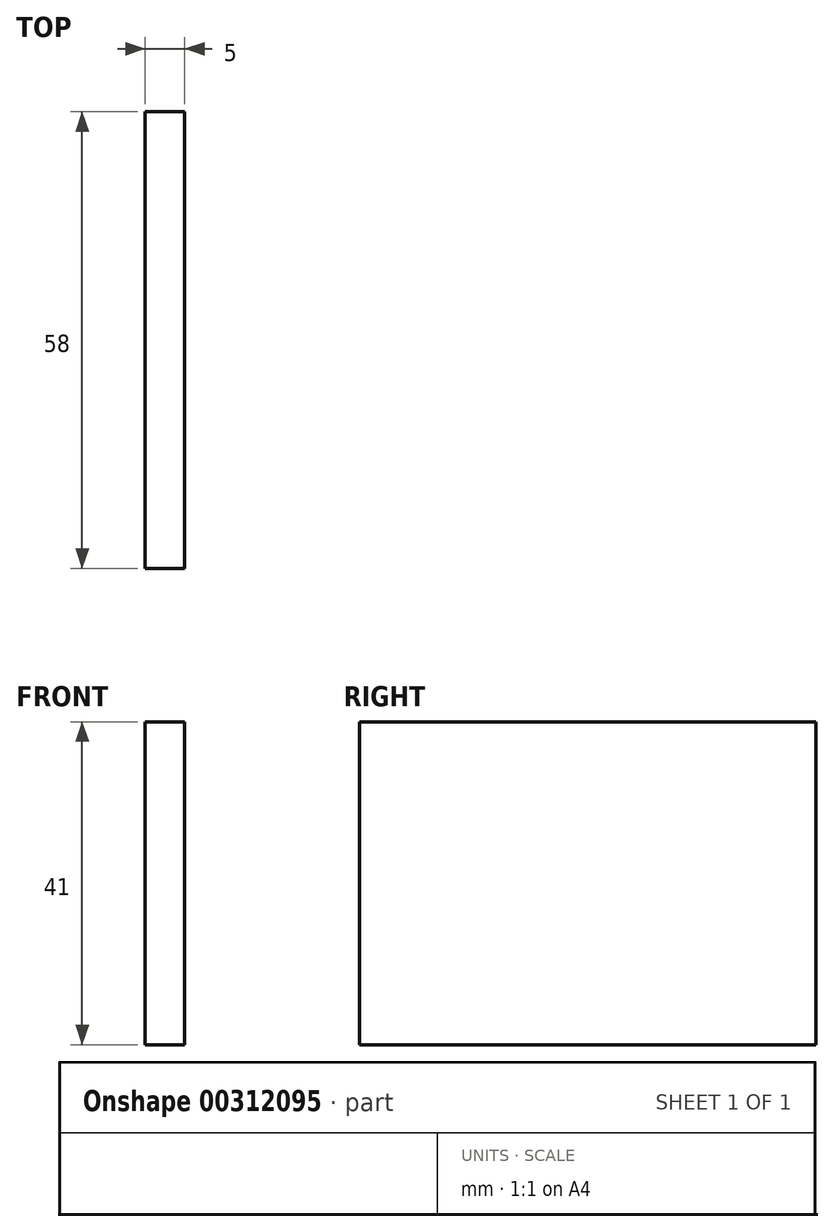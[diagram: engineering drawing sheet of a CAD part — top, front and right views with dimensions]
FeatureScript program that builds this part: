
annotation { "Feature Type Name" : "Feature", "Feature Type Description" : "" }
export const myFeature = defineFeature(function(context is Context, id is Id, definition is map)
    precondition{}
    {
        {
            var Q0;
            Q0=qCreatedBy(makeId("Front.planeOp"),FACE);
            var sketch = newSketch(context, id + "F0", { "sketchPlane" : qUnion([Q0])});
            skLineSegment(sketch, "E0.bottom", {"start": v(-2.5, 20.5) * mm, "end": v(2.5, 20.5) * mm});
            skLineSegment(sketch, "E0.top", {"start": v(-2.5, -20.5) * mm, "end": v(2.5, -20.5) * mm});
            skLineSegment(sketch, "E0.left", {"start": v(-2.5, 20.5) * mm, "end": v(-2.5, -20.5) * mm});
            skLineSegment(sketch, "E0.right", {"start": v(2.5, 20.5) * mm, "end": v(2.5, -20.5) * mm});
            skPoint(sketch, "E0.middle", {"position": v(0, 0) * mm});
            skSolve(sketch);
        }
        {
            var Q0;
            Q0 = qSketchRegion(id + "F0", true);
            extrude(context, id + "F1", {"entities" : qUnion([Q0]), "depth" : 58 * mm});
        }
    });
